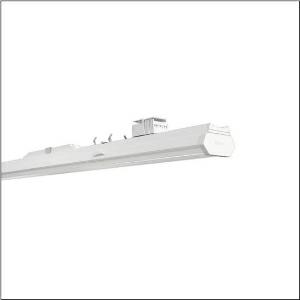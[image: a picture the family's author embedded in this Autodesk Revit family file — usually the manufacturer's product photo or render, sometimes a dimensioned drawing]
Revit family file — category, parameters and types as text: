
# Revit family: licross_r__21_protected_ho_52td11cn4c5s_1fd3
name_source: partatom
category: Lighting Fixtures
units: mm (PartAtom-declared; Revit-internal decimal feet)

## family parameters
Cut with Voids When Loaded = No
Host = Face
Light Source = No
Part Type = Normal
Room Calculation Point = No
Round Connector Dimension = Use Diameter
Shared = No

## types (1)
- --- (1 x LED, 12650 lm, 68.9 W, 4000K)
    Apparent Load = 69 VA
    CIE Flux Codes = 84 94 98 99 100
    Color Rendering = 80
    Color Temperature = 4000K
    Default Elevation = 1800 mm
    Description = Licross® 21 Protected HO, luminaire insert, of sheet steel, galvanised, coil coated, white, length: 1.500mm, width: 66mm, height: 67mm, LED rated luminous flux: 12.650lm, light colour: 840, control gear: ON/OFF Multilumen, CLOi, control gear: ECG Multilumen, with plug, 3-pole, with phase selection, mains connection: 220..240V, AC, 50/60Hz, start of lifetime: 69W, end of service life: 83W, internal wiring halogen-free, primary light control with lens, of plastic, primary optical cover: cover, of PMMA, light emission: direct distribution, primary light characteristic: symmetric, protection rating (complete): IP54, insulation class (complete): insulation class I (protective earthing), certification: CE, ENEC, VDE, UKCA, protection symbol: D if used in an environment with non-conductive dust loads with corresponding accessories, impact resistance: IK06, permissible ambient temperature for indoor applications: -35..+35°C, corresponds to IFS (International Featured Standards) requirements for safety and quality in the food industry, reducing of maximum allowable ambient temperature of 5°C with ceiling mounting, LABS conformity tested according to VDMA 24364:2018-05, packaging unit: 1 piece
    Height = 92 mm
    Lamp = 1 x LED
    Lamp Light Flux = 12650 lm
    Lamp Power = 68.9 W
    Lamp count = 1
    Length = 1500 mm
    Luminous efficacy = 184 lm/W
    Manufacturer = Siteco
    ModVariant = No
    Model = 52TD11CN4C5S
    Mounting Place = Ceiling
    Mounting Type = Pendant
    Number of Poles = 1
    OnlyDefault = Yes
    Power Factor = 1
    Product Name = Licross® 21 Protected HO
    Product group = luminaire insert | ceiling pendant
    ProductGroupID = 902
    Protection Class = Protection class I
    Protection Degree = IP 54
    RLX_Detail_Level = 1
    RLX_Emergency_Light_Flux = 0 lm
    RLX_Emergency_Type = 0
    RLX_Emergency_Type_DB = No
    RlxData = <blob elided: 22089 chars, md5=cc197d13>
    Socket = socket
    Standby Power = 0 W
    System Light Flux = 12650 lm
    System Power = 69 W
    Type Comments = factory setting: luminous flux: 100 % | (A | C | E) | 162 mA
    Type Image = l_1256148.jpg
    URL = http://relux.com
    VarID = @adj_132387
    Voltage = 0 V
    Weight = 0.00 kg
    Width = 88 mm

## geometry (parser evidence)
native form markers: Blend x4, Sweep x10
no freeform markers — native parametric forms only
